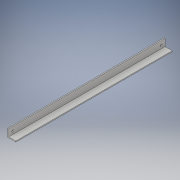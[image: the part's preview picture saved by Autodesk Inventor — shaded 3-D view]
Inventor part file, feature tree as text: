
AUTODESK INVENTOR PART (.ipt)
format: ipt  version: 2017 (Build 210142000, 142)  size: 113,152 bytes
history: native  units: in
note: dims shown in document units (in); Inventor stores cm internally (conversion verified against a paired STEP export)
features: extrude x1, hole x1, sketch x1
ambient origin geometry x8: Origin, YZ Plane, XZ Plane, XY Plane, X Axis, Y Axis, Z Axis, Center Point
bodies: Solid1 (feature_tree)
feature tree (3):
  extrude  "Extrusion1"  Depth=1.0in
  hole  "mount"  [1 undecoded]
  sketch  "Sketch7"  dims[d0=1.0in d1=1.0in d2=0.125in d3=19.375in d4=0.0in d43=0.5in d44=0.5in d45=0.7874in d47=18.375in d48=0.3937in d50=1.0in d52=0.266in d53=0.75in d54=0.507in d55=0.25in d56=0.5635in d57=1.0in d58=0.8108in]
note: 1 required parameter value undecoded (feature->parameter linkage not recoverable at this tier; creation-order binding heuristic only, values carry confidence <= 0.55)
